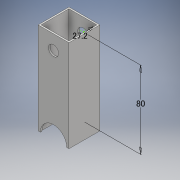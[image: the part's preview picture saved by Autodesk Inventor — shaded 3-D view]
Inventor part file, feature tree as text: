
AUTODESK INVENTOR PART (.ipt)
format: ipt  version: 2018 (Build 220112000, 112)  size: 122,880 bytes
history: native  units: mm
features: sketch x4, extrude x2, other x1, hole x1
ambient origin geometry x8: Origin, YZ Plane, XZ Plane, XY Plane, X Axis, Y Axis, Z Axis, Center Point
bodies: Body1 (feature_tree)
feature tree (8):
  other  "ソリッド1"
  extrude  "押し出し1"  Depth=32.0mm
  extrude  "押し出し2"  Depth=32.0mm
  hole  "穴1"  [1 undecoded]
  sketch  "スケッチ4"
  sketch  "スケッチ1"
  sketch  "スケッチ2"
  sketch  "スケッチ3"
note: 1 required parameter value undecoded (feature->parameter linkage not recoverable at this tier; creation-order binding heuristic only, values carry confidence <= 0.55)
